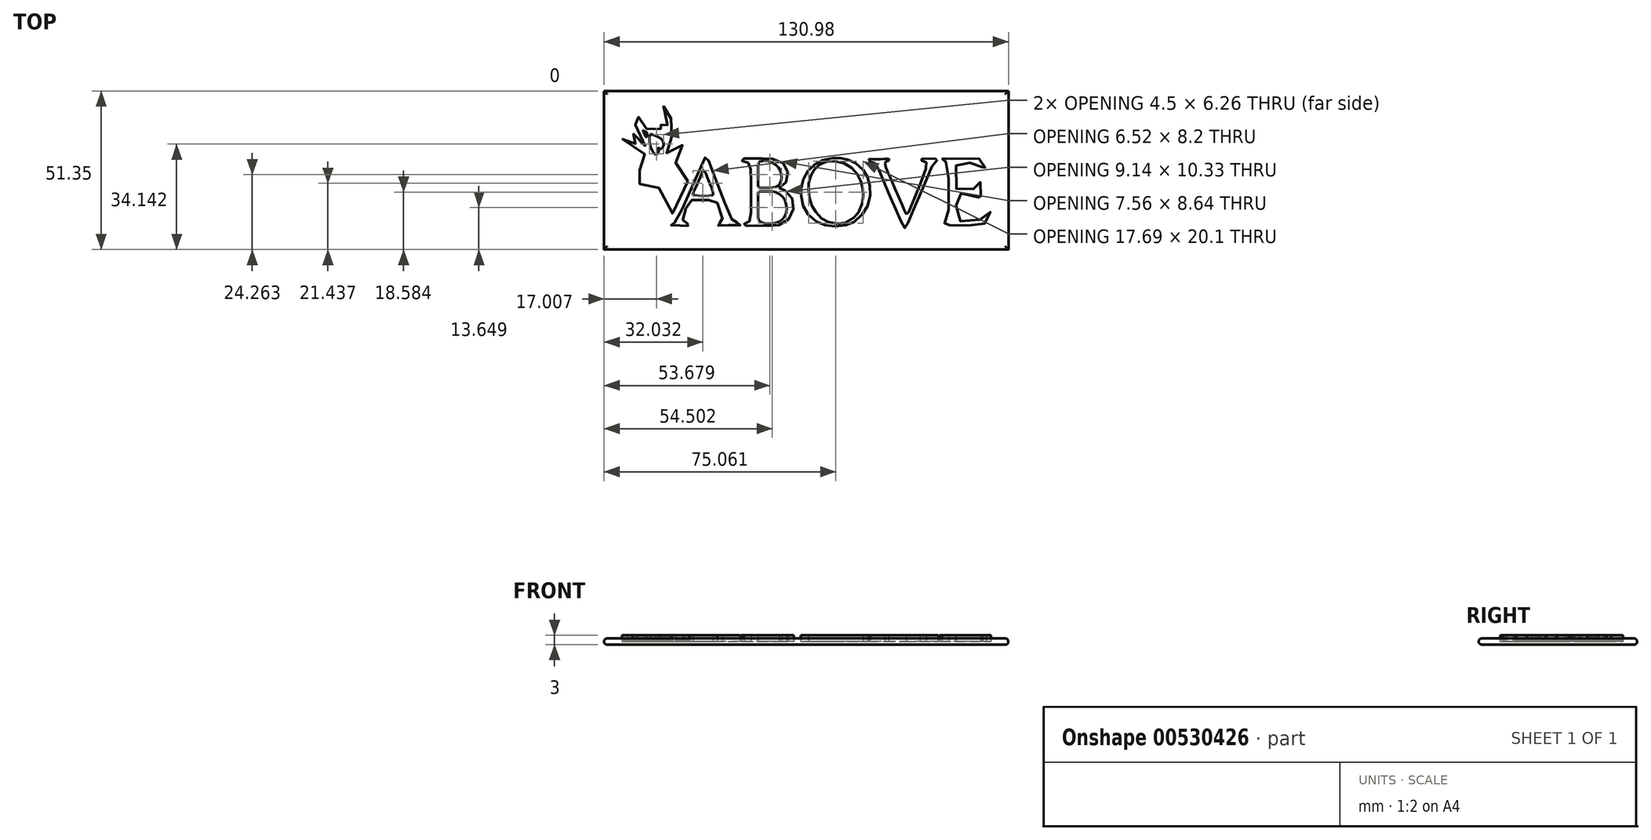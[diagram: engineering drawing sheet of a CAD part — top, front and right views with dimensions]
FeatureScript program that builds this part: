
annotation { "Feature Type Name" : "Feature", "Feature Type Description" : "" }
export const myFeature = defineFeature(function(context is Context, id is Id, definition is map)
    precondition{}
    {
        {
            var Q0;
            Q0=qCreatedBy(makeId("Top.planeOp"),FACE);
            var sketch = newSketch(context, id + "F0", { "sketchPlane" : qUnion([Q0])});
            skFitSpline(sketch, "E0", {"points": [v(-15.23, -10.3) * mm, v(-15.43, -9) * mm, v(-19.15, -4.83) * mm, v(-19.1, -4.16) * mm, v(-17.3, -2.24) * mm, v(-16.54, 0.56) * mm, v(-17.95, 2.4) * mm, v(-19.06, 2.67) * mm, v(-22.2, -1.1) * mm, v(-22.47, -0.85) * mm, v(-21.66, 0.67) * mm, v(-20.48, 3.56) * mm, v(-20.25, 7.82) * mm, v(-20.3, 10.57) * mm, v(-20.64, 10) * mm, v(-20.86, 8.89) * mm, v(-21.78, 11.53) * mm, v(-23.55, 14.33) * mm, v(-23.88, 14.2) * mm, v(-22.71, 11.12) * mm, v(-21.68, 5.35) * mm, v(-22.01, 4.8) * mm, v(-23.18, 7.18) * mm, v(-25.42, 9.31) * mm, v(-25.74, 9.34) * mm, v(-24.47, 7.53) * mm, v(-24.1, 6.22) * mm, v(-24.28, 5.66) * mm, v(-26.13, 6.06) * mm, v(-27.09, 6.34) * mm, v(-27.2, 6.66) * mm, v(-27, 8.65) * mm, v(-27.36, 8.71) * mm, v(-28, 7.01) * mm, v(-28.41, 6.66) * mm, v(-30.15, 7.44) * mm, v(-30.54, 7.72) * mm, v(-31.06, 9.57) * mm, v(-31.22, 10.63) * mm, v(-31.56, 9.76) * mm, v(-31.38, 8.06) * mm, v(-31.98, 8.26) * mm, v(-32.28, 8.06) * mm, v(-31.38, 7.34) * mm, v(-30.64, 5.1) * mm, v(-29.04, 0.34) * mm, v(-30.46, 0.54) * mm, v(-32.53, 4.69) * mm, v(-34.71, 6.38) * mm, v(-33.08, 4.32) * mm, v(-32.53, 0.83) * mm, v(-35.17, 2.24) * mm, v(-35.7, 2.77) * mm, v(-36.56, 3.39) * mm, v(-33.76, -0.17) * mm, v(-27.96, -2) * mm, v(-27.98, -3.32) * mm, v(-30.53, -6.47) * mm, v(-32.87, -8.68) * mm, v(-32.76, -10.26) * mm, v(-30.16, -11.1) * mm, v(-28.57, -10.59) * mm, v(-25.17, -11.64) * mm, v(-23.76, -15.08) * mm, v(-20.37, -20.67) * mm, v(-19.51, -19.84) * mm, v(-15.23, -10.3) * mm]});
            skFitSpline(sketch, "E1", {"points": [v(-29.8, 6.22) * mm, v(-28.73, 4.07) * mm, v(-28.53, 4.14) * mm, v(-28.4, 5.14) * mm, v(-28.49, 5.47) * mm, v(-29.63, 6.14) * mm, v(-29.8, 6.22) * mm]});
            skFitSpline(sketch, "E2", {"points": [v(-27.45, 4.88) * mm, v(-27.73, 3.04) * mm, v(-27.28, 0.78) * mm, v(-26.4, -0.9) * mm, v(-25.78, -1.63) * mm, v(-25.32, -1.6) * mm, v(-24.68, -0.86) * mm, v(-24.65, -0.6) * mm, v(-24.93, 0.18) * mm, v(-24.89, 0.58) * mm, v(-24.17, 0.18) * mm, v(-23.76, 0.32) * mm, v(-23.12, 1.2) * mm, v(-23.15, 2.37) * mm, v(-24.1, 3.66) * mm, v(-26.99, 4.92) * mm, v(-27.33, 5) * mm, v(-27.45, 4.88) * mm]});
            skSolve(sketch);
        }
        {
            var Q0;
            Q0=qSketchRegion(id+"F0",true);
            extrude(context, id + "F1", {"entities" : qUnion([Q0]), "depth" : 0.4 * mm, "offsetDistance" : 25 * mm});
        }
        {
            var Q0;
            Q0=qCreatedBy(makeId("Top.planeOp"),FACE);
            var sketch = newSketch(context, id + "F2", { "sketchPlane" : qUnion([Q0])});
            skFitSpline(sketch, "E3", {"points": [v(-17.82, -24.58) * mm, v(-20.4, -24.63) * mm, v(-20.73, -24.44) * mm, v(-20.58, -24.11) * mm, v(-19.7, -23.83) * mm, v(-18.33, -22.05) * mm, v(-9.8, -2.92) * mm, v(-9.38, -2.3) * mm, v(-8.91, -2.78) * mm, v(-6, -10.23) * mm, v(-1.17, -22.42) * mm, v(-0.56, -23.22) * mm, v(0.6, -23.64) * mm, v(1.64, -23.97) * mm, v(1.83, -24.3) * mm, v(1.5, -24.58) * mm, v(-2.53, -24.49) * mm, v(-5.2, -24.63) * mm, v(-5.63, -24.53) * mm, v(-5.72, -24.2) * mm, v(-5.02, -23.88) * mm, v(-4.17, -23.64) * mm, v(-3.99, -22.47) * mm, v(-6.05, -16.7) * mm, v(-6.85, -16.37) * mm, v(-13.83, -16.37) * mm, v(-14.4, -16.47) * mm, v(-16.79, -21.58) * mm, v(-16.79, -23.03) * mm, v(-16.32, -23.55) * mm, v(-15.1, -24.06) * mm, v(-14.63, -24.2) * mm, v(-14.68, -24.63) * mm, v(-16.7, -24.58) * mm, v(-17.82, -24.58) * mm]});
            skFitSpline(sketch, "E4", {"points": [v(-10.65, -7.65) * mm, v(-13.5, -14.08) * mm, v(-13.6, -14.6) * mm, v(-13.04, -14.87) * mm, v(-7.18, -14.83) * mm, v(-7.08, -14.5) * mm, v(-7.22, -13.42) * mm, v(-8.63, -9.76) * mm, v(-9.99, -6.76) * mm, v(-10.32, -6.76) * mm, v(-10.65, -7.65) * mm]});
            skFitSpline(sketch, "E5", {"points": [v(3, -2.92) * mm, v(10.73, -2.87) * mm, v(12, -3.01) * mm, v(14.88, -3.97) * mm, v(16.88, -6.1) * mm, v(17.2, -8.7) * mm, v(16.03, -11.17) * mm, v(14.49, -12.25) * mm, v(14.35, -12.58) * mm, v(15.19, -12.86) * mm, v(17.72, -14.5) * mm, v(18.8, -16.66) * mm, v(18.9, -19.75) * mm, v(17.3, -22.7) * mm, v(14.49, -24.4) * mm, v(11.92, -24.81) * mm, v(8.07, -24.64) * mm, v(5.08, -24.56) * mm, v(3.42, -24.71) * mm, v(3.03, -24.62) * mm, v(2.9, -24.28) * mm, v(3.1, -24.06) * mm, v(3.68, -24.02) * mm, v(4.6, -23.43) * mm, v(5.06, -21.9) * mm, v(5.21, -18.94) * mm, v(5.17, -12.14) * mm, v(5.2, -7.05) * mm, v(4.9, -5.24) * mm, v(4.43, -4.37) * mm, v(3.36, -3.74) * mm, v(2.43, -3.64) * mm, v(2.12, -3.42) * mm, v(2.18, -3.07) * mm, v(3, -2.92) * mm]});
            skFitSpline(sketch, "E6", {"points": [v(7.56, -5.2) * mm, v(7.66, -4.49) * mm, v(7.93, -4.04) * mm, v(8.5, -3.82) * mm, v(9.6, -3.72) * mm, v(11.9, -4.17) * mm, v(13.8, -5.5) * mm, v(14.9, -7.32) * mm, v(15.13, -9.05) * mm, v(14.91, -10.32) * mm, v(14.31, -11.38) * mm, v(12.84, -12.25) * mm, v(8.35, -12.43) * mm, v(7.93, -12.39) * mm, v(7.68, -12.22) * mm, v(7.54, -11.7) * mm, v(7.56, -5.2) * mm]});
            skFitSpline(sketch, "E7", {"points": [v(7.91, -13.58) * mm, v(11.85, -13.55) * mm, v(13.18, -13.78) * mm, v(14.45, -14.43) * mm, v(15.63, -15.55) * mm, v(16.13, -16.32) * mm, v(16.68, -18) * mm, v(16.73, -19.62) * mm, v(16.26, -21.4) * mm, v(15.38, -22.66) * mm, v(13.96, -23.56) * mm, v(12.42, -23.91) * mm, v(9.91, -23.87) * mm, v(8.94, -23.7) * mm, v(8.3, -23.45) * mm, v(7.71, -22.88) * mm, v(7.55, -21.97) * mm, v(7.56, -17.05) * mm, v(7.56, -14) * mm, v(7.58, -13.87) * mm, v(7.7, -13.66) * mm, v(7.91, -13.58) * mm]});
            skFitSpline(sketch, "E8", {"points": [v(31.7, -2.75) * mm, v(33.74, -2.72) * mm, v(35.38, -2.94) * mm, v(37.3, -3.53) * mm, v(39.63, -4.77) * mm, v(41.68, -6.8) * mm, v(42.85, -8.64) * mm, v(43.65, -11.01) * mm, v(43.86, -14.15) * mm, v(43.13, -17.94) * mm, v(41.96, -20.19) * mm, v(38.98, -23.16) * mm, v(36.64, -24.33) * mm, v(33.54, -24.88) * mm, v(29.86, -24.67) * mm, v(27.34, -23.85) * mm, v(24.37, -21.7) * mm, v(22.51, -19.06) * mm, v(21.56, -15.79) * mm, v(21.38, -13.38) * mm, v(21.6, -11.67) * mm, v(22.72, -8.37) * mm, v(23.86, -6.65) * mm, v(26.2, -4.52) * mm, v(28.46, -3.43) * mm, v(31.7, -2.75) * mm]});
            skFitSpline(sketch, "E9", {"points": [v(32.38, -3.76) * mm, v(35.26, -4.4) * mm, v(37.8, -5.91) * mm, v(39.49, -7.78) * mm, v(40.54, -9.6) * mm, v(41.28, -11.88) * mm, v(41.5, -13.28) * mm, v(41.51, -15.93) * mm, v(41.2, -17.67) * mm, v(40.02, -20.32) * mm, v(38.9, -21.7) * mm, v(36.42, -23.42) * mm, v(34.19, -23.98) * mm, v(31.28, -23.82) * mm, v(29.44, -23.13) * mm, v(27.67, -21.9) * mm, v(25.88, -19.86) * mm, v(25, -18.3) * mm, v(24.2, -16.04) * mm, v(23.94, -14.39) * mm, v(23.84, -12.52) * mm, v(24.02, -10.5) * mm, v(24.67, -8.26) * mm, v(25.31, -7.08) * mm, v(26.36, -5.76) * mm, v(27.76, -4.65) * mm, v(30.04, -3.86) * mm, v(32.38, -3.76) * mm]});
            skFitSpline(sketch, "E10", {"points": [v(43.45, -3.05) * mm, v(46.86, -3.14) * mm, v(49.51, -3.03) * mm, v(49.84, -3.09) * mm, v(49.97, -3.34) * mm, v(49.76, -3.62) * mm, v(49.33, -3.8) * mm, v(48.85, -4.05) * mm, v(48.66, -4.4) * mm, v(48.75, -5.26) * mm, v(49.23, -6.65) * mm, v(51.3, -11.4) * mm, v(55.34, -20.67) * mm, v(55.37, -20.75) * mm, v(55.46, -20.9) * mm], "startDerivative": vector(28.7, -1.44) * mm, "endDerivative": vector(9.03, -16.07) * mm});
            skFitSpline(sketch, "E11", {"points": [v(55.46, -20.9) * mm, v(55.42, -20.83) * mm], "startDerivative": vector(-0.04, 0.07) * mm, "endDerivative": vector(-0.04, 0.07) * mm});
            skFitSpline(sketch, "E12", {"points": [v(55.46, -20.9) * mm, v(55.54, -21.03) * mm, v(55.66, -21.12) * mm, v(55.89, -20.99) * mm, v(56.12, -20.57) * mm, v(56.33, -20.12) * mm, v(58.33, -15.36) * mm, v(60.45, -10.3) * mm, v(61.76, -6.73) * mm, v(62.08, -5.52) * mm, v(62.17, -4.73) * mm, v(62.08, -4.24) * mm, v(61.82, -3.93) * mm, v(61.35, -3.77) * mm, v(60.57, -3.59) * mm, v(60.33, -3.48) * mm, v(60.14, -3.31) * mm, v(60.16, -3.13) * mm, v(60.32, -2.99) * mm, v(60.68, -2.94) * mm, v(62.58, -3.03) * mm, v(65.59, -2.99) * mm, v(65.65, -2.99) * mm, v(65.84, -3.11) * mm, v(65.81, -3.42) * mm, v(65.4, -3.62) * mm, v(64.53, -4.24) * mm, v(63.79, -5.48) * mm, v(62.81, -7.82) * mm, v(60.31, -13.7) * mm, v(58.86, -17.15) * mm, v(57.4, -20.53) * mm, v(55.93, -24.02) * mm, v(55.57, -24.85) * mm, v(55.34, -25.26) * mm, v(55.07, -25.42) * mm, v(54.77, -25.32) * mm, v(54.42, -24.8) * mm, v(53.23, -22.02) * mm, v(52.16, -19.5) * mm, v(51.1, -17.05) * mm, v(49.81, -14.08) * mm, v(48.32, -10.6) * mm, v(46.87, -7.22) * mm, v(45.9, -5.14) * mm, v(45.4, -4.45) * mm, v(44.88, -4.06) * mm, v(44.36, -3.9) * mm, v(43.7, -3.76) * mm, v(43.26, -3.63) * mm, v(43.16, -3.56) * mm, v(43.1, -3.29) * mm, v(43.28, -3.09) * mm, v(43.45, -3.05) * mm], "startDerivative": vector(11.24, -17.17) * mm, "endDerivative": vector(21.37, 2.01) * mm});
            skFitSpline(sketch, "E13", {"points": [v(67.04, -2.88) * mm, v(72.93, -3.2) * mm, v(80.82, -2.9) * mm, v(81.01, -2.92) * mm, v(81.34, -3.25) * mm, v(81.23, -4.1) * mm, v(81.1, -5.94) * mm, v(80.98, -6.92) * mm, v(80.84, -7.23) * mm, v(80.58, -7.3) * mm, v(80.32, -7.12) * mm, v(80.3, -6.47) * mm, v(80.16, -5.59) * mm, v(79.77, -4.96) * mm, v(79.06, -4.54) * mm, v(77.64, -4.32) * mm, v(75.81, -4.27) * mm, v(72.82, -4.27) * mm, v(72.2, -4.35) * mm, v(71.8, -4.6) * mm, v(71.63, -5.13) * mm, v(71.6, -6.58) * mm, v(71.62, -12.25) * mm, v(71.67, -12.6) * mm, v(71.81, -12.82) * mm, v(72.31, -12.9) * mm, v(75.15, -12.9) * mm, v(76.93, -12.82) * mm, v(78.03, -12.6) * mm, v(78.56, -12.33) * mm, v(78.95, -11.5) * mm, v(79.07, -10.94) * mm, v(79.2, -10.66) * mm, v(79.5, -10.57) * mm, v(79.74, -10.81) * mm, v(79.72, -11.77) * mm, v(79.65, -12.85) * mm, v(79.63, -14.83) * mm, v(79.75, -16.4) * mm, v(79.72, -16.72) * mm, v(79.5, -16.87) * mm, v(79.18, -16.76) * mm, v(79.03, -16.34) * mm, v(78.85, -15.54) * mm, v(78.5, -14.88) * mm, v(77.81, -14.45) * mm, v(77.2, -14.32) * mm, v(72.62, -14.27) * mm, v(72.05, -14.35) * mm, v(71.74, -14.52) * mm, v(71.61, -14.98) * mm, v(71.62, -15.64) * mm, v(71.61, -21.73) * mm, v(71.78, -22.56) * mm, v(71.96, -22.89) * mm, v(72.43, -23.14) * mm, v(73.82, -23.32) * mm, v(76.16, -23.27) * mm, v(78.46, -22.93) * mm, v(80.04, -22.42) * mm, v(81.02, -21.9) * mm, v(81.9, -21.16) * mm, v(82.43, -20.44) * mm, v(82.68, -20.25) * mm, v(82.94, -20.36) * mm, v(82.99, -20.9) * mm, v(82.63, -21.97) * mm, v(81.71, -23.27) * mm, v(80.37, -24.35) * mm, v(79.08, -24.74) * mm, v(77.24, -24.73) * mm, v(75.47, -24.58) * mm, v(73.07, -24.45) * mm, v(71.23, -24.45) * mm, v(69.24, -24.53) * mm, v(67.96, -24.7) * mm, v(67.43, -24.72) * mm, v(67.14, -24.58) * mm, v(67.1, -24.26) * mm, v(67.44, -24.02) * mm, v(68.36, -23.75) * mm, v(68.97, -23.1) * mm, v(69.2, -22.19) * mm, v(69.23, -21.12) * mm, v(69.23, -16.3) * mm, v(69.23, -11) * mm, v(69.22, -6.69) * mm, v(69.15, -5.8) * mm, v(68.82, -4.54) * mm, v(68.34, -3.97) * mm, v(67.58, -3.67) * mm, v(66.86, -3.6) * mm, v(66.5, -3.55) * mm, v(66.36, -3.33) * mm, v(66.58, -2.95) * mm, v(67.04, -2.88) * mm]});
            skSolve(sketch);
        }
        {
            var Q0;
            Q0 = qSketchRegion(id + "F2", true);
            extrude(context, id + "F3", {"entities" : qUnion([Q0]), "depth" : 2 * mm, "offsetDistance" : 25 * mm});
        }
        {
            var Q0;
            Q0=qCreatedBy(makeId("Top.planeOp"),FACE);
            var sketch = newSketch(context, id + "F4", { "sketchPlane" : qUnion([Q0])});
            skLineSegment(sketch, "E14.bottom", {"start": v(-42.37, 18.96) * mm, "end": v(88.6, 18.96) * mm});
            skLineSegment(sketch, "E14.top", {"start": v(-42.37, -32.4) * mm, "end": v(88.6, -32.4) * mm});
            skLineSegment(sketch, "E14.left", {"start": v(-42.37, 18.96) * mm, "end": v(-42.37, -32.4) * mm});
            skLineSegment(sketch, "E14.right", {"start": v(88.6, 18.96) * mm, "end": v(88.6, -32.4) * mm});
            skSolve(sketch);
        }
        {
            var Q0;
            Q0 = qSketchRegion(id + "F4", true);
            extrude(context, id + "F5", {"entities" : qUnion([Q0]), "endBound" : BoundingType.SYMMETRIC, "depth" : 2 * mm, "offsetDistance" : 25 * mm});
        }
        {
            var Q0;
            Q0=makeQuery(id+"F5.opExtrude","CAP_FACE",FACE,{"disambiguationData":[OSD([sQuery(id+"F4.wireOp",EDGE,"E14.bottom"),sQuery(id+"F4.wireOp",EDGE,"E14.top"),sQuery(id+"F4.wireOp",EDGE,"E14.left"),sQuery(id+"F4.wireOp",EDGE,"E14.right")])],"isStart":false});
            var Q1;
            Q1=makeQuery(id+"F5.opExtrude","CAP_FACE",FACE,{"disambiguationData":[OSD([sQuery(id+"F4.wireOp",EDGE,"E14.bottom"),sQuery(id+"F4.wireOp",EDGE,"E14.top"),sQuery(id+"F4.wireOp",EDGE,"E14.left"),sQuery(id+"F4.wireOp",EDGE,"E14.right")])],"isStart":true});
            fillet(context, id + "F6", {"entities" : qUnion([Q0, Q1]), "radius" : 1 * mm, "tangentPropagation" : true, "allowEdgeOverflow" : false});
        }
        {
            var Q0;
            Q0 = qSketchRegion(id + "F0", true);
            extrude(context, id + "F7", {"entities" : qUnion([Q0]), "depth" : 2 * mm, "offsetDistance" : 25 * mm});
        }
    });
